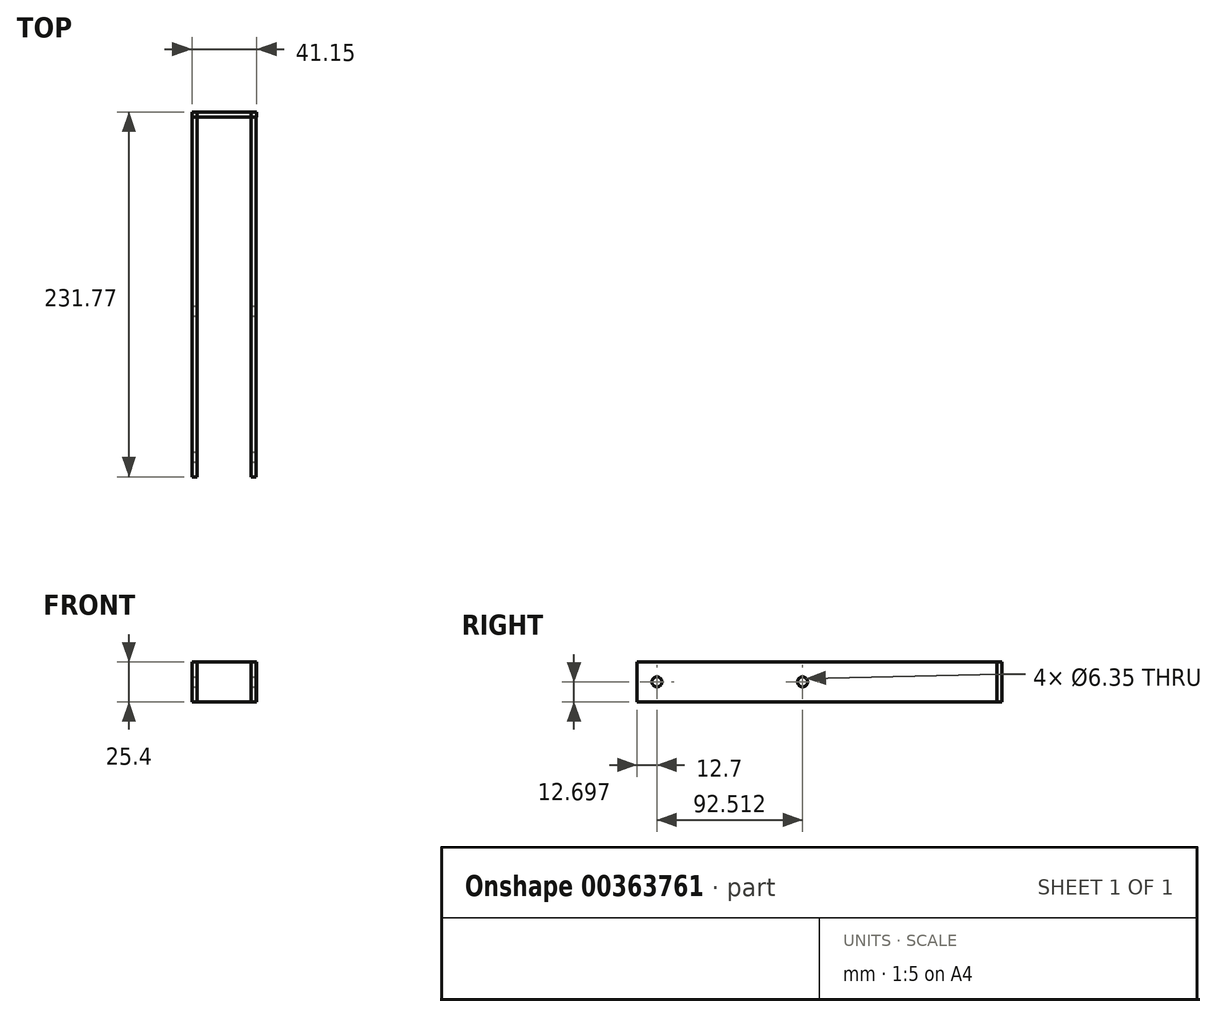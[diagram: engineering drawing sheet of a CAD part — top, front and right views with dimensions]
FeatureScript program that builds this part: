
annotation { "Feature Type Name" : "Feature", "Feature Type Description" : "" }
export const myFeature = defineFeature(function(context is Context, id is Id, definition is map)
    precondition{}
    {
        {
            var Q0;
            Q0=qCreatedBy(makeId("Front.planeOp"),FACE);
            var sketch = newSketch(context, id + "F0", { "sketchPlane" : qUnion([Q0])});
            skLineSegment(sketch, "E0.bottom", {"start": v(-43.87, 7.89) * mm, "end": v(-3.23, 7.89) * mm});
            skLineSegment(sketch, "E0.top", {"start": v(-43.87, -17.51) * mm, "end": v(-3.23, -17.51) * mm});
            skLineSegment(sketch, "E0.left", {"start": v(-43.87, 7.89) * mm, "end": v(-43.87, -17.51) * mm});
            skLineSegment(sketch, "E0.right", {"start": v(-3.23, 7.89) * mm, "end": v(-3.23, -17.51) * mm});
            skLineSegment(sketch, "E1", {"start": v(-6.4, 7.89) * mm, "end": v(-6.4, -17.51) * mm});
            skLineSegment(sketch, "E2", {"start": v(-40.7, 7.89) * mm, "end": v(-40.7, -17.51) * mm});
            skSolve(sketch);
        }
        {
            var Q0;
            {var subQ0=sQuery(id+"F0.wireOp",EDGE,"E0.left");Q0=makeQuery(id+"F0.imprint","IMPRINT",FACE,{"disambiguationData":[TD([[makeQuery(id+"F0.imprint","IMPRINT",EDGE,{"derivedFrom":subQ0}),1.0]])]});}
            extrude(context, id + "F1", {"entities" : qUnion([Q0]), "depth" : 228.6 * mm});
        }
        {
            var Q0;
            {var subQ0=sQuery(id+"F0.wireOp",EDGE,"E0.right");Q0=makeQuery(id+"F0.imprint","IMPRINT",FACE,{"disambiguationData":[TD([[makeQuery(id+"F0.imprint","IMPRINT",EDGE,{"derivedFrom":subQ0}),-1.0]])]});}
            extrude(context, id + "F2", {"entities" : qUnion([Q0]), "depth" : 228.6 * mm});
        }
        {
            var Q0;
            {var subQ0=sQuery(id+"F0.wireOp",EDGE,"E1");Q0=makeQuery(id+"F0.imprint","IMPRINT",FACE,{"disambiguationData":[TD([[makeQuery(id+"F0.imprint","IMPRINT",EDGE,{"derivedFrom":subQ0}),-1.0]])]});}
            extrude(context, id + "F3", {"entities" : qUnion([Q0]), "oppositeDirection" : true, "depth" : 3.17 * mm});
        }
        {
            var Q0;
            Q0=makeQuery(id+"F3.opExtrude","SWEPT_FACE",FACE,{"disambiguationData":[OSD([sQuery(id+"F0.wireOp",EDGE,"E1")])]});
            extrude(context, id + "F4", {"entities" : qUnion([Q0]), "depth" : 3.56 * mm});
        }
        {
            var Q0;
            Q0=makeQuery(id+"F3.opExtrude","SWEPT_FACE",FACE,{"disambiguationData":[OSD([sQuery(id+"F0.wireOp",EDGE,"E2")])]});
            extrude(context, id + "F5", {"entities" : qUnion([Q0]), "depth" : 3.3 * mm});
        }
        {
            var Q0;
            Q0=makeQuery(id+"F2.opExtrude","SWEPT_FACE",FACE,{"disambiguationData":[OSD([sQuery(id+"F0.wireOp",EDGE,"E0.right")])]});
            var sketch = newSketch(context, id + "F6", { "sketchPlane" : qUnion([Q0])});
            skLineSegment(sketch, "E3", {"start": v(-228.6, -4.81) * mm, "end": v(3.38, -4.81) * mm, "construction": true});
            skCircle(sketch, "E4", {"center": v(-215.9, -4.81) * mm, "radius": 3.18 * mm});
            skCircle(sketch, "E5", {"center": v(-123.39, -4.81) * mm, "radius": 3.18 * mm});
            skSolve(sketch);
        }
        {
            var Q0;
            Q0=makeQuery(id+"F6.imprint","IMPRINT",FACE,{"disambiguationData":[TD([[makeQuery(id+"F6.imprint","IMPRINT",EDGE,{"derivedFrom":sQuery(id+"F6.wireOp",EDGE,"E5")}),1.0]])]});
            var Q1;
            Q1=makeQuery(id+"F6.imprint","IMPRINT",FACE,{"disambiguationData":[TD([[makeQuery(id+"F6.imprint","IMPRINT",EDGE,{"derivedFrom":sQuery(id+"F6.wireOp",EDGE,"E4")}),1.0]])]});
            extrude(context, id + "F7", {"entities" : qUnion([Q0, Q1]), "operationType" : NewBodyOperationType.REMOVE, "endBound" : BoundingType.THROUGH_ALL, "oppositeDirection" : true, "depth" : 25.4 * mm});
        }
    });
